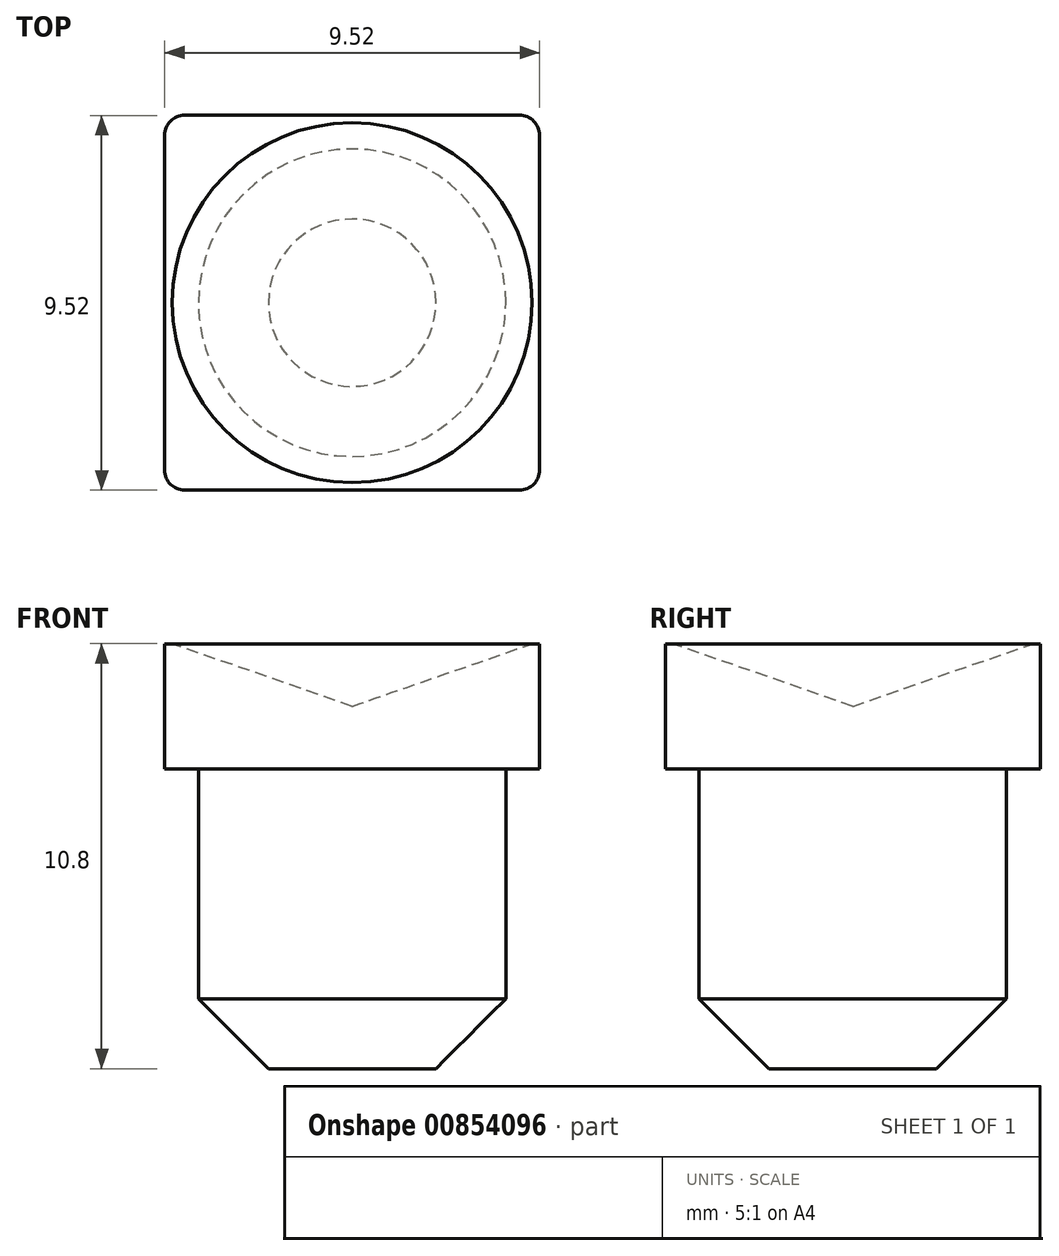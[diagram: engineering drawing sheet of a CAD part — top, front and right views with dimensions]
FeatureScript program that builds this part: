
annotation { "Feature Type Name" : "Feature", "Feature Type Description" : "" }
export const myFeature = defineFeature(function(context is Context, id is Id, definition is map)
    precondition{}
    {
        {
            var Q0;
            Q0=qCreatedBy(makeId("Top.planeOp"),FACE);
            var sketch = newSketch(context, id + "F0", { "sketchPlane" : qUnion([Q0])});
            skCircle(sketch, "E0", {"center": v(0, 0) * mm, "radius": 3.9 * mm});
            skSolve(sketch);
        }
        {
            var Q0;
            Q0=makeQuery(id+"F0.imprint","IMPRINT",FACE,{"disambiguationData":[TD([[makeQuery(id+"F0.imprint","IMPRINT",EDGE,{"derivedFrom":sQuery(id+"F0.wireOp",EDGE,"E0")}),1.0]])]});
            extrude(context, id + "F1", {"entities" : qUnion([Q0]), "oppositeDirection" : true, "depth" : 7.62 * mm, "offsetDistance" : 25.4 * mm});
        }
        {
            var Q0;
            Q0=makeQuery(id+"F1.opExtrude","CAP_FACE",FACE,{"disambiguationData":[OSD([sQuery(id+"F0.wireOp",EDGE,"E0")])],"isStart":true});
            var sketch = newSketch(context, id + "F2", { "sketchPlane" : qUnion([Q0])});
            skLineSegment(sketch, "E1.bottom", {"start": v(4.76, 4.76) * mm, "end": v(-4.76, 4.76) * mm});
            skLineSegment(sketch, "E1.top", {"start": v(4.76, -4.76) * mm, "end": v(-4.76, -4.76) * mm});
            skLineSegment(sketch, "E1.left", {"start": v(4.76, 4.76) * mm, "end": v(4.76, -4.76) * mm});
            skLineSegment(sketch, "E1.right", {"start": v(-4.76, 4.76) * mm, "end": v(-4.76, -4.76) * mm});
            skPoint(sketch, "E1.middle", {"position": v(0, 0) * mm});
            skSolve(sketch);
        }
        {
            var Q0;
            Q0 = qSketchRegion(id + "F2", true);
            extrude(context, id + "F3", {"entities" : qUnion([Q0]), "operationType" : NewBodyOperationType.ADD, "depth" : 3.17 * mm, "offsetDistance" : 25.4 * mm});
        }
        {
            var Q0;
            Q0=qCreatedBy(makeId("Front.planeOp"),FACE);
            var sketch = newSketch(context, id + "F4", { "sketchPlane" : qUnion([Q0])});
            skLineSegment(sketch, "E2.0.2", {"start": v(4.57, 3.18) * mm, "end": v(0, 3.18) * mm});
            skLineSegment(sketch, "E3", {"start": v(0, 1.59) * mm, "end": v(0, 3.18) * mm});
            skPoint(sketch, "E4.orphan", {"position": v(-4.76, 3.18) * mm});
            skLineSegment(sketch, "E5", {"start": v(4.57, 3.17) * mm, "end": v(0, 1.59) * mm});
            skSolve(sketch);
        }
        {
            var Q0;
            Q0=makeQuery(id+"F4.imprint","IMPRINT",FACE,{"disambiguationData":[TD([[makeQuery(id+"F4.imprint","IMPRINT",EDGE,{"derivedFrom":sQuery(id+"F4.wireOp",EDGE,"E2.0.2")}),1.0]])]});
            var Q1;
            Q1=sQuery(id+"F4.wireOp",EDGE,"E3");
            revolve(context, id + "F5", {"operationType" : NewBodyOperationType.REMOVE, "surfaceOperationType" : NewSurfaceOperationType.NEW, "entities" : qUnion([Q0]), "axis" : qUnion([Q1]), "revolveType" : RevolveType.FULL, "oppositeDirection" : true});
        }
        {
            var Q0;
            Q0=makeQuery(id+"F3.opExtrude","SWEPT_EDGE",EDGE,{"disambiguationData":[OSD([sQuery(id+"F2.wireOp",EDGE,"E1.bottom"),sQuery(id+"F2.wireOp",EDGE,"E1.right")])]});
            var Q1;
            Q1=makeQuery(id+"F3.opExtrude","SWEPT_EDGE",EDGE,{"disambiguationData":[OSD([sQuery(id+"F2.wireOp",EDGE,"E1.bottom"),sQuery(id+"F2.wireOp",EDGE,"E1.left")])]});
            var Q2;
            Q2=makeQuery(id+"F3.opExtrude","SWEPT_EDGE",EDGE,{"disambiguationData":[OSD([sQuery(id+"F2.wireOp",EDGE,"E1.top"),sQuery(id+"F2.wireOp",EDGE,"E1.right")])]});
            var Q3;
            Q3=makeQuery(id+"F3.opExtrude","SWEPT_EDGE",EDGE,{"disambiguationData":[OSD([sQuery(id+"F2.wireOp",EDGE,"E1.top"),sQuery(id+"F2.wireOp",EDGE,"E1.left")])]});
            fillet(context, id + "F6", {"entities" : qUnion([Q0, Q1, Q2, Q3]), "radius" : 0.5 * mm, "tangentPropagation" : true, "allowEdgeOverflow" : false});
        }
        {
            var Q0;
            Q0=makeQuery(id+"F1.opExtrude","CAP_EDGE",EDGE,{"disambiguationData":[OSD([sQuery(id+"F0.wireOp",EDGE,"E0")])],"isStart":false});
            chamfer(context, id + "F7", {"entities" : qUnion([Q0]), "width" : 1.78 * mm, "tangentPropagation" : true});
        }
    });
